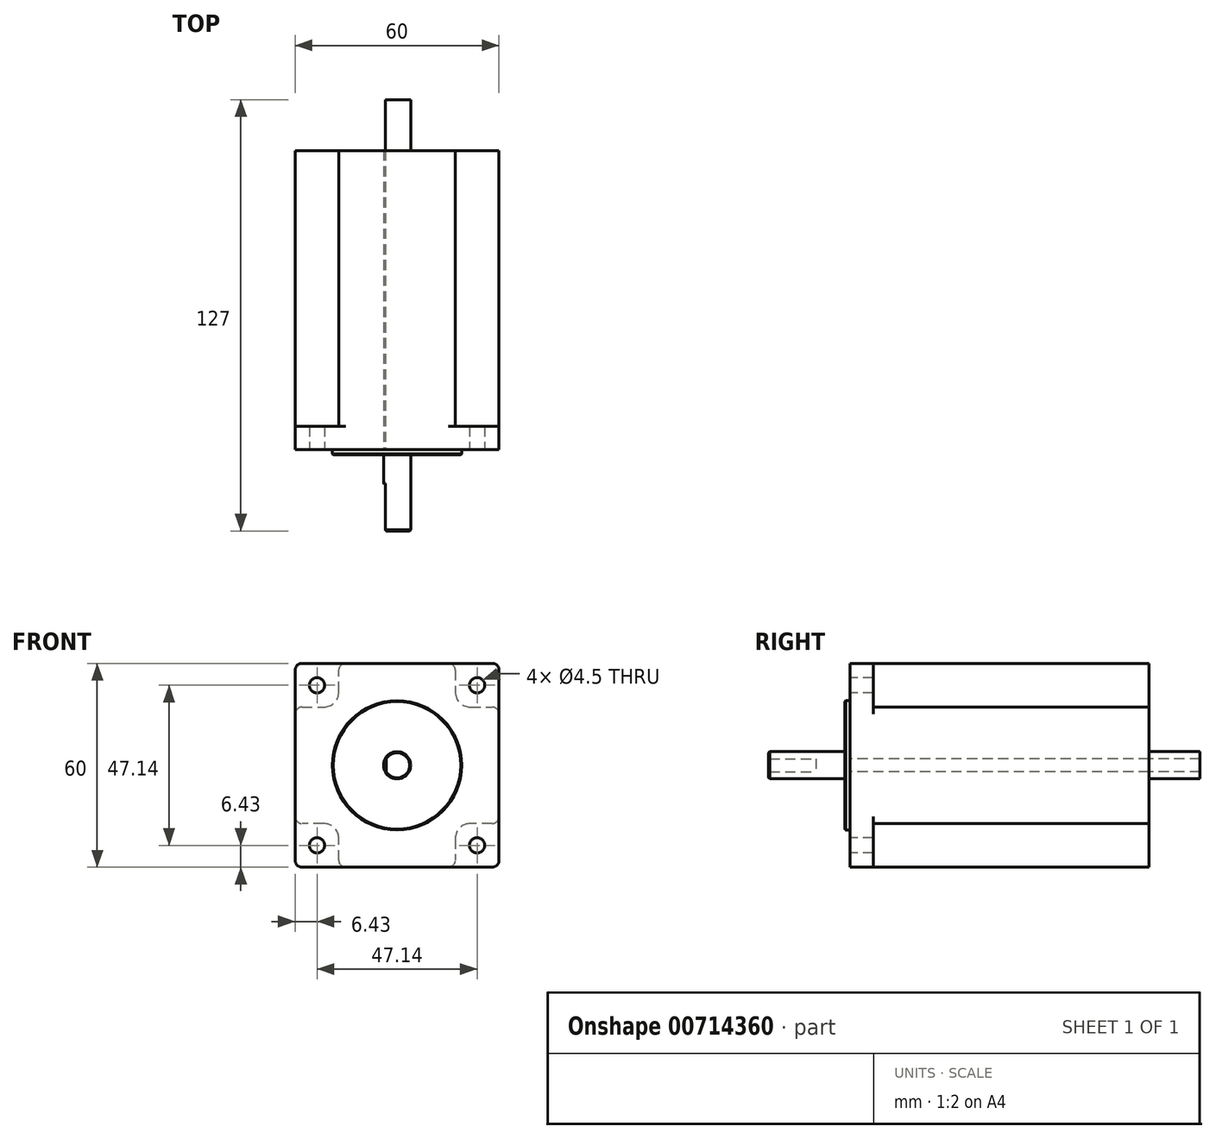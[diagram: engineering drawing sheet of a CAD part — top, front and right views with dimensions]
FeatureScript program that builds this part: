
annotation { "Feature Type Name" : "Feature", "Feature Type Description" : "" }
export const myFeature = defineFeature(function(context is Context, id is Id, definition is map)
    precondition{}
    {
        {
            var Q0;
            Q0=qCreatedBy(makeId("Front.planeOp"),FACE);
            var sketch = newSketch(context, id + "F0", { "sketchPlane" : qUnion([Q0])});
            skLineSegment(sketch, "E0.bottom", {"start": v(30, -30) * mm, "end": v(-30, -30) * mm});
            skLineSegment(sketch, "E0.top", {"start": v(30, 30) * mm, "end": v(-30, 30) * mm});
            skLineSegment(sketch, "E0.left", {"start": v(30, -30) * mm, "end": v(30, 30) * mm});
            skLineSegment(sketch, "E0.right", {"start": v(-30, -30) * mm, "end": v(-30, 30) * mm});
            skPoint(sketch, "E0.middle", {"position": v(0, 0) * mm});
            skCircle(sketch, "E1", {"center": v(-23.57, 23.57) * mm, "radius": 2.25 * mm});
            skCircle(sketch, "E2.0.1.0", {"center": v(-23.57, -23.57) * mm, "radius": 2.25 * mm});
            skCircle(sketch, "E2.1.0.0", {"center": v(23.57, 23.57) * mm, "radius": 2.25 * mm});
            skCircle(sketch, "E2.1.1.0", {"center": v(23.57, -23.57) * mm, "radius": 2.25 * mm});
            skLineSegment(sketch, "E2.direction1", {"start": v(-23.57, 23.57) * mm, "end": v(23.57, 23.57) * mm, "construction": true});
            skLineSegment(sketch, "E2.direction2", {"start": v(-23.57, 23.57) * mm, "end": v(-23.57, -23.57) * mm, "construction": true});
            skLineSegment(sketch, "E3", {"start": v(0, 0) * mm, "end": v(0, 6.9) * mm, "construction": true});
            skLineSegment(sketch, "E4", {"start": v(0, 0) * mm, "end": v(8.18, 0) * mm, "construction": true});
            skCircle(sketch, "E5", {"center": v(0, 0) * mm, "radius": 19.05 * mm});
            skLineSegment(sketch, "E6", {"start": v(-30, 17.14) * mm, "end": v(-17.14, 17.14) * mm});
            skLineSegment(sketch, "E7", {"start": v(-17.14, 17.14) * mm, "end": v(-17.14, 30) * mm});
            skLineSegment(sketch, "E8.1.0", {"start": v(-17.14, -17.14) * mm, "end": v(-30, -17.14) * mm});
            skLineSegment(sketch, "E8.1.1", {"start": v(-17.14, -30) * mm, "end": v(-17.14, -17.14) * mm});
            skLineSegment(sketch, "E8.2.0", {"start": v(17.14, -17.14) * mm, "end": v(17.14, -30) * mm});
            skLineSegment(sketch, "E8.2.1", {"start": v(30, -17.14) * mm, "end": v(17.14, -17.14) * mm});
            skLineSegment(sketch, "E8.3.0", {"start": v(17.14, 17.14) * mm, "end": v(30, 17.14) * mm});
            skLineSegment(sketch, "E8.3.1", {"start": v(17.14, 30) * mm, "end": v(17.14, 17.14) * mm});
            skCircle(sketch, "E9", {"center": v(0, 0) * mm, "radius": 4 * mm});
            skLineSegment(sketch, "E10", {"start": v(-3.5, 1.94) * mm, "end": v(-3.5, -1.94) * mm});
            skSolve(sketch);
        }
        {
            var Q0;
            Q0 = qSketchRegion(id + "F0", true);
            var Q1;
            Q1=makeQuery(id+"F0.imprint","IMPRINT",FACE,{"disambiguationData":[TD([[makeQuery(id+"F0.imprint","IMPRINT",EDGE,{"derivedFrom":sQuery(id+"F0.wireOp",EDGE,"E5")}),1.0]])]});
            extrude(context, id + "F1", {"entities" : qUnion([Q0, Q1]), "oppositeDirection" : true, "depth" : 6.8 * mm, "offsetDistance" : 25 * mm});
        }
        {
            var Q0;
            Q0=makeQuery(id+"F0.imprint","IMPRINT",FACE,{"disambiguationData":[TD([[makeQuery(id+"F0.imprint","IMPRINT",EDGE,{"derivedFrom":sQuery(id+"F0.wireOp",EDGE,"E5")}),1.0]])]});
            extrude(context, id + "F2", {"entities" : qUnion([Q0]), "operationType" : NewBodyOperationType.ADD, "depth" : 1.6 * mm, "offsetDistance" : 25 * mm});
        }
        {
            var Q0;
            Q0=makeQuery(id+"F0.imprint","IMPRINT",FACE,{"disambiguationData":[TD([[makeQuery(id+"F0.imprint","IMPRINT",EDGE,{"derivedFrom":sQuery(id+"F0.wireOp",EDGE,"E5")}),-1.0]])]});
            var Q1;
            Q1=makeQuery(id+"F0.imprint","IMPRINT",FACE,{"disambiguationData":[TD([[makeQuery(id+"F0.imprint","IMPRINT",EDGE,{"derivedFrom":sQuery(id+"F0.wireOp",EDGE,"E5")}),1.0]])]});
            extrude(context, id + "F3", {"entities" : qUnion([Q0, Q1]), "operationType" : NewBodyOperationType.ADD, "oppositeDirection" : true, "depth" : 88 * mm, "offsetDistance" : 25 * mm});
        }
        {
            var Q0;
            Q0=makeQuery(id+"F3.opExtrude","SWEPT_EDGE",EDGE,{"disambiguationData":[OSD([sQuery(id+"F0.wireOp",EDGE,"E8.3.0"),sQuery(id+"F0.wireOp",EDGE,"E8.3.1")])]});
            var Q1;
            Q1=makeQuery(id+"F3.opExtrude","SWEPT_EDGE",EDGE,{"disambiguationData":[OSD([sQuery(id+"F0.wireOp",EDGE,"E8.2.0"),sQuery(id+"F0.wireOp",EDGE,"E8.2.1")])]});
            var Q2;
            Q2=makeQuery(id+"F3.opExtrude","SWEPT_EDGE",EDGE,{"disambiguationData":[OSD([sQuery(id+"F0.wireOp",EDGE,"E6"),sQuery(id+"F0.wireOp",EDGE,"E7")])]});
            var Q3;
            Q3=makeQuery(id+"F3.opExtrude","SWEPT_EDGE",EDGE,{"disambiguationData":[OSD([sQuery(id+"F0.wireOp",EDGE,"E8.1.0"),sQuery(id+"F0.wireOp",EDGE,"E8.1.1")])]});
            fillet(context, id + "F4", {"entities" : qUnion([Q0, Q1, Q2, Q3]), "radius" : 4.45 * mm, "tangentPropagation" : true, "allowEdgeOverflow" : false});
        }
        {
            var Q0;
            Q0=makeQuery(id+"F1.opExtrude","SWEPT_EDGE",EDGE,{"disambiguationData":[OSD([sQuery(id+"F0.wireOp",EDGE,"E0.top"),sQuery(id+"F0.wireOp",EDGE,"E0.right")])]});
            var Q1;
            Q1=makeQuery(id+"F1.opExtrude","SWEPT_EDGE",EDGE,{"disambiguationData":[OSD([sQuery(id+"F0.wireOp",EDGE,"E0.top"),sQuery(id+"F0.wireOp",EDGE,"E0.left")])]});
            var Q2;
            Q2=makeQuery(id+"F3.opExtrude","SWEPT_EDGE",EDGE,{"disambiguationData":[OSD([sQuery(id+"F0.wireOp",EDGE,"E0.top"),sQuery(id+"F0.wireOp",EDGE,"E7")])]});
            var Q3;
            Q3=makeQuery(id+"F3.opExtrude","SWEPT_EDGE",EDGE,{"disambiguationData":[OSD([sQuery(id+"F0.wireOp",EDGE,"E0.right"),sQuery(id+"F0.wireOp",EDGE,"E6")])]});
            var Q4;
            Q4=makeQuery(id+"F3.opExtrude","SWEPT_EDGE",EDGE,{"disambiguationData":[OSD([sQuery(id+"F0.wireOp",EDGE,"E0.top"),sQuery(id+"F0.wireOp",EDGE,"E8.3.1")])]});
            var Q5;
            Q5=makeQuery(id+"F1.opExtrude","SWEPT_EDGE",EDGE,{"disambiguationData":[OSD([sQuery(id+"F0.wireOp",EDGE,"E0.bottom"),sQuery(id+"F0.wireOp",EDGE,"E0.right")])]});
            var Q6;
            Q6=makeQuery(id+"F1.opExtrude","SWEPT_EDGE",EDGE,{"disambiguationData":[OSD([sQuery(id+"F0.wireOp",EDGE,"E0.bottom"),sQuery(id+"F0.wireOp",EDGE,"E0.left")])]});
            var Q7;
            Q7=makeQuery(id+"F3.opExtrude","SWEPT_EDGE",EDGE,{"disambiguationData":[OSD([sQuery(id+"F0.wireOp",EDGE,"E0.left"),sQuery(id+"F0.wireOp",EDGE,"E8.3.0")])]});
            var Q8;
            Q8=makeQuery(id+"F3.opExtrude","SWEPT_EDGE",EDGE,{"disambiguationData":[OSD([sQuery(id+"F0.wireOp",EDGE,"E0.left"),sQuery(id+"F0.wireOp",EDGE,"E8.2.1")])]});
            var Q9;
            Q9=makeQuery(id+"F3.opExtrude","SWEPT_EDGE",EDGE,{"disambiguationData":[OSD([sQuery(id+"F0.wireOp",EDGE,"E0.bottom"),sQuery(id+"F0.wireOp",EDGE,"E8.2.0")])]});
            var Q10;
            Q10=makeQuery(id+"F3.opExtrude","SWEPT_EDGE",EDGE,{"disambiguationData":[OSD([sQuery(id+"F0.wireOp",EDGE,"E0.bottom"),sQuery(id+"F0.wireOp",EDGE,"E8.1.1")])]});
            var Q11;
            Q11=makeQuery(id+"F3.opExtrude","SWEPT_EDGE",EDGE,{"disambiguationData":[OSD([sQuery(id+"F0.wireOp",EDGE,"E0.right"),sQuery(id+"F0.wireOp",EDGE,"E8.1.0")])]});
            fillet(context, id + "F5", {"entities" : qUnion([Q0, Q1, Q2, Q3, Q4, Q5, Q6, Q7, Q8, Q9, Q10, Q11]), "radius" : 2 * mm, "tangentPropagation" : true, "allowEdgeOverflow" : false});
        }
        {
            var Q0;
            {var subQ0=sQuery(id+"F0.wireOp",EDGE,"E10");Q0=makeQuery(id+"F0.imprint","IMPRINT",FACE,{"disambiguationData":[TD([[makeQuery(id+"F0.imprint","IMPRINT",EDGE,{"derivedFrom":subQ0}),-1.0]])]});}
            extrude(context, id + "F6", {"entities" : qUnion([Q0]), "operationType" : NewBodyOperationType.ADD, "depth" : 10 * mm, "offsetDistance" : 25 * mm});
        }
        {
            var Q0;
            {var subQ0=sQuery(id+"F0.wireOp",EDGE,"E10");Q0=makeQuery(id+"F0.imprint","IMPRINT",FACE,{"disambiguationData":[TD([[makeQuery(id+"F0.imprint","IMPRINT",EDGE,{"derivedFrom":subQ0}),1.0]])]});}
            extrude(context, id + "F7", {"entities" : qUnion([Q0]), "operationType" : NewBodyOperationType.ADD, "depth" : 24 * mm, "offsetDistance" : 25 * mm});
        }
        {
            var Q0;
            {var subQ0=sQuery(id+"F0.wireOp",EDGE,"E10");Q0=makeQuery(id+"F0.imprint","IMPRINT",FACE,{"disambiguationData":[TD([[makeQuery(id+"F0.imprint","IMPRINT",EDGE,{"derivedFrom":subQ0}),1.0]])]});}
            extrude(context, id + "F8", {"entities" : qUnion([Q0]), "operationType" : NewBodyOperationType.ADD, "oppositeDirection" : true, "depth" : (88 + 15) * mm, "offsetDistance" : 25 * mm});
        }
        {
            var Q0;
            Q0=makeQuery(id+"F7.opExtrude","CAP_EDGE",EDGE,{"disambiguationData":[OSD([sQuery(id+"F0.wireOp",EDGE,"E9")])],"isStart":false});
            var Q1;
            Q1=makeQuery(id+"F7.opExtrude","CAP_EDGE",EDGE,{"disambiguationData":[OSD([sQuery(id+"F0.wireOp",EDGE,"E10")])],"isStart":false});
            var Q2;
            Q2=makeQuery(id+"F2.opExtrude","CAP_EDGE",EDGE,{"disambiguationData":[OSD([sQuery(id+"F0.wireOp",EDGE,"E5")])],"isStart":false});
            chamfer(context, id + "F9", {"entities" : qUnion([Q0, Q1, Q2]), "width" : .3 * mm, "tangentPropagation" : true});
        }
    });
